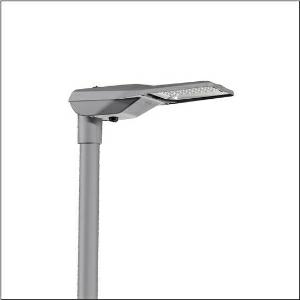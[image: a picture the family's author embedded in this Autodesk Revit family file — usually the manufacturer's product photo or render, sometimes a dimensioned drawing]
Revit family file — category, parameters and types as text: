
# Revit family: streetlight_sl_21_mini___stw1_0a_5xe2e33t08hb_df53
name_source: partatom
category: Lighting Fixtures
units: mm (PartAtom-declared; Revit-internal decimal feet)

## family parameters
Cut with Voids When Loaded = No
Host = Face
Light Source = No
Part Type = Normal
Room Calculation Point = No
Round Connector Dimension = Use Diameter
Shared = No

## types (1)
- --- (1 x LED, 9040 lm, 66 W, 3000K)
    Apparent Load = 66 VA
    CIE Flux Codes = 38 75 98 100 100
    Color Rendering = 70
    Color Temperature = 3000K
    Default Elevation = 1800 mm
    Description = Streetlight SL 21 mini, mast luminaire, primary light control with lens, of PMMA, primary optical cover: cover, of toughened safety glass, transparent, light distribution: STW1.0a, light emission: direct distribution, primary light characteristic: asymmetric, installation type: side-entry, post-top, LED, High Power LED, rated luminous flux: 9.040lm, luminous efficacy: 137lm/W, light colour: 730, colour temperature: 3000K, control gear: D4i, control: overheat protection, constant luminous flux control, time-dependent luminous flux control, flexible luminous flux parameterisation, pre-setting: logarithmic dimming characteristic, mains connection: 220..240V, AC, 50/60Hz, start of lifetime: 66W, end of service life: 69W, reduction: 30W, luminaire housing, of diecast aluminium, powder-coated, SITECO metallic grey (DB 702S), corrosivity category C5 high according to DIN EN ISO 12944, please order mast flange separately, inclination adjustable: 0°, 5°, 10°, 15°, sealing non-destructively replaceable, multi-level sealing system, length: 628mm, width: 235mm, height: 110mm, mast flange for spigot size: 42mm (side-entry): 5XC10008XM4, 60/48mm (side-entry/post-top): 5XC10108XM2, 76/60mm (side-entry/post-top): 5XC10108XM1, mounting height: 4..8m, Smart Interface below and above, protection rating (complete): IP66, insulation class (complete): insulation class II (safety insulation), certification: CE, ENEC, ENEC+, VDE, impact resistance: IK10, permissible operating ambient temperature for outdoor applications: -40..+50°C, standard-compliant lighting for roads and squares, packaging unit: 1 piece

Light Distribution: STW1.0a
    Height = 110 mm
    Lamp = 1 x LED
    Lamp Light Flux = 9040 lm
    Lamp Power = 66 W
    Lamp count = 1
    Length = 625 mm
    Luminous efficacy = 137 lm/W
    Manufacturer = Siteco
    ModVariant = No
    Model = 5XE2E33T08HB
    Number of Poles = 1
    OnlyDefault = Yes
    Power Factor = 1
    Product Name = Streetlight SL 21 mini | STW1.0a
    Product group = mast luminaire | pylon top
    ProductGroupID = 6100
    Protection Class = Protection class II
    Protection Degree = IP 66
    RLX_Detail_Level = 1
    RLX_Emergency_Light_Flux = 0 lm
    RLX_Emergency_Type = 0
    RLX_Emergency_Type_DB = No
    RlxData = <blob elided: 26337 chars, md5=c1178d80>
    Socket = socket
    Standby Power = 0 W
    System Light Flux = 9040 lm
    System Power = 66 W
    Type Comments = factory setting: luminous flux: 100 % | dim-lin: 254 | 670 mA
    Type Image = l_1003514.jpg
    URL = http://relux.com
    VarID = @adj_184651
    Voltage = 0 V
    Weight = 0.00 kg
    Width = 234 mm

## geometry (parser evidence)
native form markers: Blend x4, Sweep x11
no freeform markers — native parametric forms only
